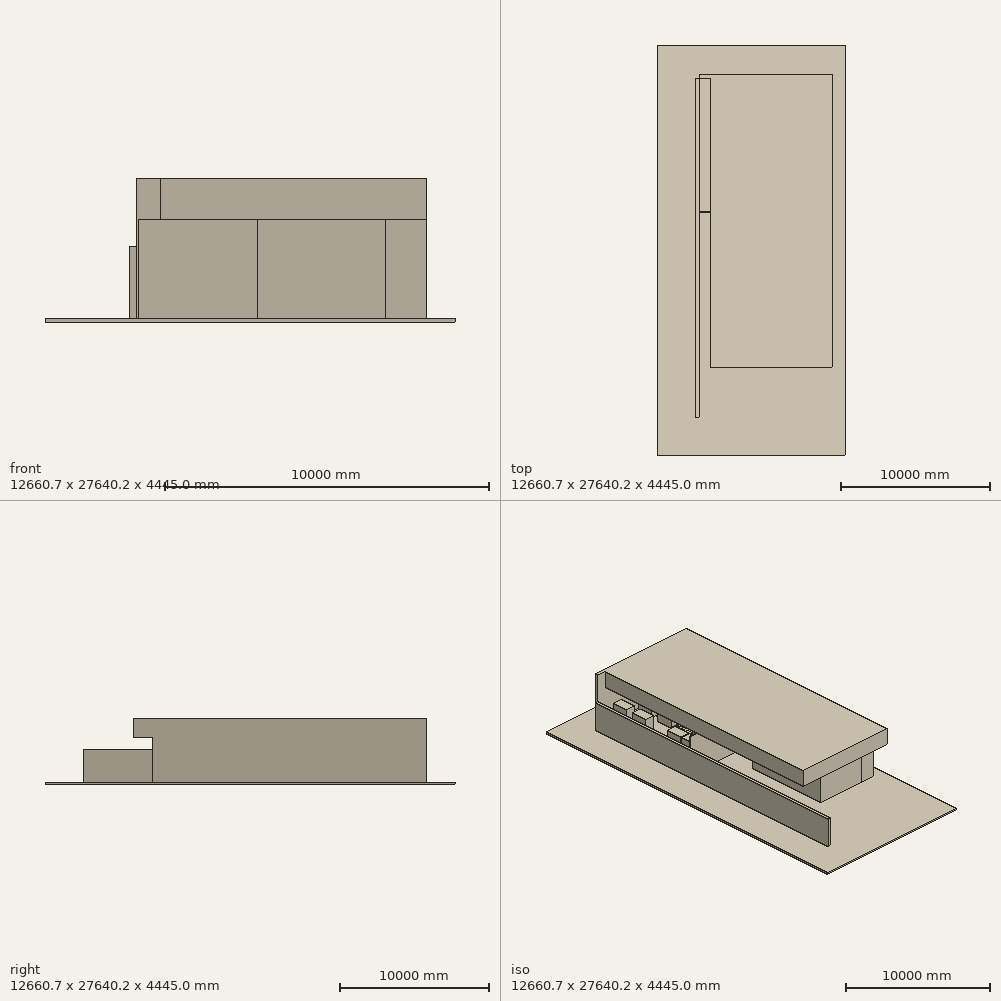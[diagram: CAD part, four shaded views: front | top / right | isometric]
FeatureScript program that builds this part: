
annotation { "Feature Type Name" : "Feature", "Feature Type Description" : "" }
export const myFeature = defineFeature(function(context is Context, id is Id, definition is map)
    precondition{}
    {
        {
            var Q0;
            Q0=qCreatedBy(makeId("Top.planeOp"),FACE);
            var sketch = newSketch(context, id + "F0", { "sketchPlane" : qUnion([Q0])});
            skLineSegment(sketch, "E0.bottom", {"start": v(0, 0) * mm, "end": v(3962.4, 0) * mm});
            skLineSegment(sketch, "E0.right", {"start": v(3962.4, 0) * mm, "end": v(3962.4, 100.58) * mm});
            skLineSegment(sketch, "E1.bottom", {"start": v(0, -9144) * mm, "end": v(3962.4, -9144) * mm});
            skLineSegment(sketch, "E1.top", {"start": v(0, -2438.4) * mm, "end": v(3962.4, -2438.4) * mm});
            skLineSegment(sketch, "E1.left", {"start": v(0, -2438.4) * mm, "end": v(0, -9144) * mm});
            skLineSegment(sketch, "E1.right", {"start": v(3962.4, -2438.4) * mm, "end": v(3962.4, -9144) * mm});
            skLineSegment(sketch, "E2", {"start": v(0, 100.58) * mm, "end": v(3962.4, 100.58) * mm});
            skLineSegment(sketch, "E3", {"start": v(0, 0) * mm, "end": v(0, 100.58) * mm});
            skLineSegment(sketch, "E4", {"start": v(0, 0) * mm, "end": v(-3657.6, 0) * mm});
            skLineSegment(sketch, "E5", {"start": v(-3657.6, 0) * mm, "end": v(-3657.6, 100.58) * mm});
            skLineSegment(sketch, "E6", {"start": v(-3657.6, 100.58) * mm, "end": v(0, 100.58) * mm});
            skSolve(sketch);
        }
        {
            var Q0;
            Q0=qSketchRegion(id+"F0",true);
            extrude(context, id + "F1", {"entities" : qUnion([Q0]), "depth" : 3048 * mm});
        }
        {
            var Q0;
            Q0=qCreatedBy(makeId("Top.planeOp"),FACE);
            var sketch = newSketch(context, id + "F2", { "sketchPlane" : qUnion([Q0])});
            skLineSegment(sketch, "E7.bottom", {"start": v(-3718.56, 9040.37) * mm, "end": v(3962.4, 9040.37) * mm});
            skLineSegment(sketch, "E7.top", {"start": v(-3718.56, 9284.2) * mm, "end": v(3962.4, 9284.2) * mm});
            skLineSegment(sketch, "E7.left", {"start": v(-3718.56, 9040.37) * mm, "end": v(-3718.56, 9284.2) * mm});
            skLineSegment(sketch, "E7.right", {"start": v(3962.4, 9040.37) * mm, "end": v(3962.4, 9284.2) * mm});
            skLineSegment(sketch, "E8.bottom", {"start": v(-3718.56, 9040.37) * mm, "end": v(-3962.4, 9040.37) * mm});
            skLineSegment(sketch, "E8.top", {"start": v(-3718.56, -13819.63) * mm, "end": v(-3962.4, -13819.63) * mm});
            skLineSegment(sketch, "E8.left", {"start": v(-3718.56, 9040.37) * mm, "end": v(-3718.56, -13819.63) * mm});
            skLineSegment(sketch, "E8.right", {"start": v(-3962.4, 9040.37) * mm, "end": v(-3962.4, -13819.63) * mm});
            skSolve(sketch);
        }
        {
            var Q0;
            Q0=qSketchRegion(id+"F2",true);
            extrude(context, id + "F3", {"entities" : qUnion([Q0]), "depth" : 2212.85 * mm});
        }
        {
            var Q0;
            Q0=makeQuery(id+"F1.opExtrude","CAP_FACE",FACE,{"disambiguationData":[OSD([sQuery(id+"F0.wireOp",EDGE,"E0.bottom"),sQuery(id+"F0.wireOp",EDGE,"E0.top"),sQuery(id+"F0.wireOp",EDGE,"E0.left"),sQuery(id+"F0.wireOp",EDGE,"E0.right")])],"isStart":false});
            var sketch = newSketch(context, id + "F4", { "sketchPlane" : qUnion([Q0])});
            skLineSegment(sketch, "E9.bottom", {"start": v(3962.4, 9284.2) * mm, "end": v(-2990.09, 9284.2) * mm});
            skLineSegment(sketch, "E9.top", {"start": v(3962.4, -10436.35) * mm, "end": v(-2990.09, -10436.35) * mm});
            skLineSegment(sketch, "E9.left", {"start": v(3962.4, 9284.2) * mm, "end": v(3962.4, -10436.35) * mm});
            skLineSegment(sketch, "E9.right", {"start": v(-2990.09, 9284.2) * mm, "end": v(-2990.09, -10436.35) * mm});
            skSolve(sketch);
        }
        {
            var Q0;
            Q0=qSketchRegion(id+"F4",true);
            extrude(context, id + "F5", {"entities" : qUnion([Q0]), "depth" : 1270 * mm});
        }
        {
            var Q0;
            Q0=makeQuery(id+"F1.opExtrude","SWEPT_FACE",FACE,{"disambiguationData":[OSD([sQuery(id+"F0.wireOp",EDGE,"E1.right")])]});
            var sketch = newSketch(context, id + "F6", { "sketchPlane" : qUnion([Q0])});
            skLineSegment(sketch, "E10.bottom", {"start": v(-9144, 0) * mm, "end": v(9284.2, 0) * mm});
            skLineSegment(sketch, "E10.top", {"start": v(-9144, 4318) * mm, "end": v(9284.2, 4318) * mm});
            skLineSegment(sketch, "E10.left", {"start": v(-9144, 0) * mm, "end": v(-9144, 3048) * mm});
            skLineSegment(sketch, "E10.right", {"start": v(9284.2, 0) * mm, "end": v(9284.2, 4318) * mm});
            skLineSegment(sketch, "E11.bottom", {"start": v(-9144, 4318) * mm, "end": v(-10436.35, 4318) * mm});
            skLineSegment(sketch, "E11.top", {"start": v(-9144, 3048) * mm, "end": v(-10436.35, 3048) * mm});
            skLineSegment(sketch, "E11.right", {"start": v(-10436.35, 4318) * mm, "end": v(-10436.35, 3048) * mm});
            skSolve(sketch);
        }
        {
            var Q0;
            Q0=qSketchRegion(id+"F6",true);
            extrude(context, id + "F7", {"entities" : qUnion([Q0]), "depth" : 1270 * mm});
        }
        {
            var Q0;
            Q0=qCreatedBy(makeId("Top.planeOp"),FACE);
            var sketch = newSketch(context, id + "F8", { "sketchPlane" : qUnion([Q0])});
            skLineSegment(sketch, "E12.bottom", {"start": v(6117.86, 11268.55) * mm, "end": v(-6542.87, 11268.55) * mm});
            skLineSegment(sketch, "E12.top", {"start": v(6117.86, -16371.62) * mm, "end": v(-6542.87, -16371.62) * mm});
            skLineSegment(sketch, "E12.left", {"start": v(6117.86, 11268.55) * mm, "end": v(6117.86, -16371.62) * mm});
            skLineSegment(sketch, "E12.right", {"start": v(-6542.87, 11268.55) * mm, "end": v(-6542.87, -16371.62) * mm});
            skSolve(sketch);
        }
        {
            var Q0;
            Q0=qSketchRegion(id+"F8",true);
            extrude(context, id + "F9", {"entities" : qUnion([Q0]), "oppositeDirection" : true, "depth" : 127 * mm});
        }
        {
            var Q0;
            Q0=makeQuery(id+"F3.opExtrude","CAP_FACE",FACE,{"disambiguationData":[OSD([sQuery(id+"F2.wireOp",EDGE,"E7.bottom"),sQuery(id+"F2.wireOp",EDGE,"E7.top"),sQuery(id+"F2.wireOp",EDGE,"E7.left"),sQuery(id+"F2.wireOp",EDGE,"E7.right")])],"isStart":false});
            var sketch = newSketch(context, id + "F10", { "sketchPlane" : qUnion([Q0])});
            skLineSegment(sketch, "E13.bottom", {"start": v(-3718.56, 9284.2) * mm, "end": v(3962.4, 9284.2) * mm});
            skLineSegment(sketch, "E13.top", {"start": v(-3718.56, 9040.37) * mm, "end": v(3962.4, 9040.37) * mm});
            skLineSegment(sketch, "E13.left", {"start": v(-3718.56, 9284.2) * mm, "end": v(-3718.56, 9040.37) * mm});
            skLineSegment(sketch, "E13.right", {"start": v(3962.4, 9284.2) * mm, "end": v(3962.4, 9040.37) * mm});
            skSolve(sketch);
        }
        {
            var Q0;
            Q0=qSketchRegion(id+"F10",true);
            var Q1;
            Q1=makeQuery(id+"F5.opExtrude","CAP_FACE",FACE,{"disambiguationData":[OSD([sQuery(id+"F4.wireOp",EDGE,"E9.bottom"),sQuery(id+"F4.wireOp",EDGE,"E9.top"),sQuery(id+"F4.wireOp",EDGE,"E9.left"),sQuery(id+"F4.wireOp",EDGE,"E9.right")])],"isStart":false});
            extrude(context, id + "F11", {"entities" : qUnion([Q0]), "operationType" : NewBodyOperationType.ADD, "endBound" : BoundingType.UP_TO_SURFACE, "endBoundEntityFace" : qUnion([Q1]), "depth" : 25.4 * mm});
        }
        {
            var Q0;
            Q0=qCreatedBy(makeId("Top.planeOp"),FACE);
            var sketch = newSketch(context, id + "F12", { "sketchPlane" : qUnion([Q0])});
            skLineSegment(sketch, "E14.bottom", {"start": v(-2499.36, 710.18) * mm, "end": v(-1724.66, 710.18) * mm});
            skLineSegment(sketch, "E14.top", {"start": v(-2499.36, 2005.58) * mm, "end": v(-1724.66, 2005.58) * mm});
            skLineSegment(sketch, "E14.left", {"start": v(-2499.36, 710.18) * mm, "end": v(-2499.36, 2005.58) * mm});
            skLineSegment(sketch, "E14.right", {"start": v(-1724.66, 710.18) * mm, "end": v(-1724.66, 2005.58) * mm});
            skLineSegment(sketch, "E15.bottom", {"start": v(-2499.36, 2107.18) * mm, "end": v(-1724.66, 2107.18) * mm});
            skLineSegment(sketch, "E15.top", {"start": v(-2499.36, 3402.58) * mm, "end": v(-1724.66, 3402.58) * mm});
            skLineSegment(sketch, "E15.left", {"start": v(-2499.36, 2107.18) * mm, "end": v(-2499.36, 3402.58) * mm});
            skLineSegment(sketch, "E15.right", {"start": v(-1724.66, 2107.18) * mm, "end": v(-1724.66, 3402.58) * mm});
            skLineSegment(sketch, "E16.bottom", {"start": v(-2499.36, 5535.17) * mm, "end": v(-1724.66, 5535.17) * mm});
            skLineSegment(sketch, "E16.top", {"start": v(-2499.36, 6830.57) * mm, "end": v(-1724.66, 6830.57) * mm});
            skLineSegment(sketch, "E16.left", {"start": v(-2499.36, 5535.17) * mm, "end": v(-2499.36, 6830.57) * mm});
            skLineSegment(sketch, "E16.right", {"start": v(-1724.66, 5535.17) * mm, "end": v(-1724.66, 6830.57) * mm});
            skLineSegment(sketch, "E17.bottom", {"start": v(-35.56, 6830.57) * mm, "end": v(739.14, 6830.57) * mm});
            skLineSegment(sketch, "E17.top", {"start": v(-35.56, 5535.17) * mm, "end": v(739.14, 5535.17) * mm});
            skLineSegment(sketch, "E17.left", {"start": v(-35.56, 6830.57) * mm, "end": v(-35.56, 5535.17) * mm});
            skLineSegment(sketch, "E17.right", {"start": v(739.14, 6830.57) * mm, "end": v(739.14, 5535.17) * mm});
            skLineSegment(sketch, "E18.bottom", {"start": v(-35.56, 3402.58) * mm, "end": v(739.14, 3402.58) * mm});
            skLineSegment(sketch, "E18.top", {"start": v(-35.56, 2107.18) * mm, "end": v(739.14, 2107.18) * mm});
            skLineSegment(sketch, "E18.left", {"start": v(-35.56, 3402.58) * mm, "end": v(-35.56, 2107.18) * mm});
            skLineSegment(sketch, "E18.right", {"start": v(739.14, 3402.58) * mm, "end": v(739.14, 2107.18) * mm});
            skLineSegment(sketch, "E19.bottom", {"start": v(-35.56, 2005.58) * mm, "end": v(739.14, 2005.58) * mm});
            skLineSegment(sketch, "E19.top", {"start": v(-35.56, 710.18) * mm, "end": v(739.14, 710.18) * mm});
            skLineSegment(sketch, "E19.left", {"start": v(-35.56, 2005.58) * mm, "end": v(-35.56, 710.18) * mm});
            skLineSegment(sketch, "E19.right", {"start": v(739.14, 2005.58) * mm, "end": v(739.14, 710.18) * mm});
            skLineSegment(sketch, "E20.bottom", {"start": v(2665.63, 7031.21) * mm, "end": v(3414.93, 7031.21) * mm});
            skLineSegment(sketch, "E20.top", {"start": v(2665.63, 8631.41) * mm, "end": v(3414.93, 8631.41) * mm});
            skLineSegment(sketch, "E20.left", {"start": v(2665.63, 7031.21) * mm, "end": v(2665.63, 8631.41) * mm});
            skLineSegment(sketch, "E20.right", {"start": v(3414.93, 7031.21) * mm, "end": v(3414.93, 8631.41) * mm});
            skLineSegment(sketch, "E21.bottom", {"start": v(-2499.36, 7440.17) * mm, "end": v(-1724.66, 7440.17) * mm});
            skLineSegment(sketch, "E21.top", {"start": v(-2499.36, 8735.57) * mm, "end": v(-1724.66, 8735.57) * mm});
            skLineSegment(sketch, "E21.left", {"start": v(-2499.36, 7440.17) * mm, "end": v(-2499.36, 8735.57) * mm});
            skLineSegment(sketch, "E21.right", {"start": v(-1724.66, 7440.17) * mm, "end": v(-1724.66, 8735.57) * mm});
            skLineSegment(sketch, "E22.bottom", {"start": v(-35.56, 7440.17) * mm, "end": v(739.14, 7440.17) * mm});
            skLineSegment(sketch, "E22.top", {"start": v(-35.56, 8735.57) * mm, "end": v(739.14, 8735.57) * mm});
            skLineSegment(sketch, "E22.left", {"start": v(-35.56, 7440.17) * mm, "end": v(-35.56, 8735.57) * mm});
            skLineSegment(sketch, "E22.right", {"start": v(739.14, 7440.17) * mm, "end": v(739.14, 8735.57) * mm});
            skLineSegment(sketch, "E23", {"start": v(-2004.06, 963.1) * mm, "end": v(-2004.06, 3910.58) * mm});
            skArc(sketch, "E24", {"start": v(-2004.06, 3910.58) * mm, "mid": v(-1922.23, 4108.15) * mm, "end": v(-1724.66, 4189.98) * mm});
            skLineSegment(sketch, "E25", {"start": v(-2004.06, 963.1) * mm, "end": v(-1800.86, 963.1) * mm});
            skLineSegment(sketch, "E26", {"start": v(-1800.86, 963.1) * mm, "end": v(-1800.86, 3910.58) * mm});
            skArc(sketch, "E27", {"start": v(-1800.86, 3910.58) * mm, "mid": v(-1778.54, 3964.47) * mm, "end": v(-1724.66, 3986.78) * mm});
            skLineSegment(sketch, "E28", {"start": v(-1724.66, 3986.78) * mm, "end": v(3872.3, 3986.78) * mm});
            skLineSegment(sketch, "E29", {"start": v(-1724.66, 4189.98) * mm, "end": v(3872.3, 4189.98) * mm});
            skLineSegment(sketch, "E30", {"start": v(-1778.54, 3964.47) * mm, "end": v(-1922.23, 4108.15) * mm, "construction": true});
            skLineSegment(sketch, "E31", {"start": v(-2423.16, 3139.03) * mm, "end": v(-2219.96, 3139.03) * mm});
            skLineSegment(sketch, "E32", {"start": v(-2219.96, 3139.03) * mm, "end": v(-2219.96, 4139.18) * mm});
            skArc(sketch, "E33", {"start": v(-2219.96, 4139.18) * mm, "mid": v(-2197.64, 4193.07) * mm, "end": v(-2143.76, 4215.38) * mm});
            skLineSegment(sketch, "E34", {"start": v(-2423.16, 3139.03) * mm, "end": v(-2423.16, 4139.18) * mm});
            skArc(sketch, "E35", {"start": v(-2423.16, 4139.18) * mm, "mid": v(-2341.33, 4336.75) * mm, "end": v(-2143.76, 4418.58) * mm});
            skLineSegment(sketch, "E36", {"start": v(-2143.76, 4215.38) * mm, "end": v(3879.27, 4215.38) * mm});
            skLineSegment(sketch, "E37", {"start": v(3879.27, 4215.38) * mm, "end": v(3879.27, 4418.58) * mm});
            skLineSegment(sketch, "E38", {"start": v(3879.27, 4418.58) * mm, "end": v(-2143.76, 4418.58) * mm});
            skLineSegment(sketch, "E39", {"start": v(-2197.64, 4193.07) * mm, "end": v(-2341.33, 4336.75) * mm, "construction": true});
            skLineSegment(sketch, "E40", {"start": v(459.74, 993.21) * mm, "end": v(459.74, 3453.38) * mm});
            skArc(sketch, "E41", {"start": v(459.74, 3453.38) * mm, "mid": v(541.57, 3650.95) * mm, "end": v(739.14, 3732.78) * mm});
            skLineSegment(sketch, "E42", {"start": v(459.74, 993.21) * mm, "end": v(662.94, 993.21) * mm});
            skLineSegment(sketch, "E43", {"start": v(662.94, 993.21) * mm, "end": v(662.94, 3453.38) * mm});
            skArc(sketch, "E44", {"start": v(662.94, 3453.38) * mm, "mid": v(685.26, 3507.27) * mm, "end": v(739.14, 3529.58) * mm});
            skLineSegment(sketch, "E45", {"start": v(739.14, 3529.58) * mm, "end": v(3914.38, 3529.58) * mm});
            skLineSegment(sketch, "E46", {"start": v(739.14, 3732.78) * mm, "end": v(3914.38, 3732.78) * mm});
            skLineSegment(sketch, "E47", {"start": v(685.26, 3507.27) * mm, "end": v(541.57, 3650.95) * mm, "construction": true});
            skLineSegment(sketch, "E48", {"start": v(40.64, 3024.4) * mm, "end": v(243.84, 3024.4) * mm});
            skLineSegment(sketch, "E49", {"start": v(243.84, 3024.4) * mm, "end": v(243.84, 3681.98) * mm});
            skArc(sketch, "E50", {"start": v(243.84, 3681.98) * mm, "mid": v(266.16, 3735.87) * mm, "end": v(320.04, 3758.18) * mm});
            skLineSegment(sketch, "E51", {"start": v(40.64, 3024.4) * mm, "end": v(40.64, 3681.98) * mm});
            skArc(sketch, "E52", {"start": v(40.64, 3681.98) * mm, "mid": v(122.47, 3879.55) * mm, "end": v(320.04, 3961.38) * mm});
            skLineSegment(sketch, "E53", {"start": v(320.04, 3758.18) * mm, "end": v(3899.59, 3758.18) * mm});
            skLineSegment(sketch, "E54", {"start": v(3899.59, 3758.18) * mm, "end": v(3899.59, 3961.38) * mm});
            skLineSegment(sketch, "E55", {"start": v(3899.59, 3961.38) * mm, "end": v(320.04, 3961.38) * mm});
            skLineSegment(sketch, "E56", {"start": v(266.16, 3735.87) * mm, "end": v(122.47, 3879.55) * mm, "construction": true});
            skLineSegment(sketch, "E57", {"start": v(3914.38, 3732.78) * mm, "end": v(3914.38, 3529.58) * mm});
            skLineSegment(sketch, "E58", {"start": v(3872.3, 3986.78) * mm, "end": v(3872.3, 4189.98) * mm});
            skLineSegment(sketch, "E59", {"start": v(-1832.37, 4443.98) * mm, "end": v(4264.41, 4443.98) * mm});
            skArc(sketch, "E60.MirrorCS", {"start": v(-2219.96, 4748.78) * mm, "mid": v(-2197.64, 4694.9) * mm, "end": v(-2143.76, 4672.58) * mm});
            skArc(sketch, "E61.MirrorCS", {"start": v(662.94, 5434.58) * mm, "mid": v(685.26, 5380.7) * mm, "end": v(739.14, 5358.38) * mm});
            skArc(sketch, "E62.MirrorCS", {"start": v(243.84, 5205.98) * mm, "mid": v(266.16, 5152.1) * mm, "end": v(320.04, 5129.78) * mm});
            skLineSegment(sketch, "E63.MirrorCS", {"start": v(3899.59, 5129.78) * mm, "end": v(3899.59, 4926.58) * mm});
            skLineSegment(sketch, "E64.MirrorCS", {"start": v(3879.27, 4672.58) * mm, "end": v(3879.27, 4469.38) * mm});
            skLineSegment(sketch, "E65.MirrorCS", {"start": v(3914.38, 5155.18) * mm, "end": v(3914.38, 5358.38) * mm});
            skLineSegment(sketch, "E66.MirrorCS", {"start": v(685.26, 5380.7) * mm, "end": v(541.57, 5237.02) * mm, "construction": true});
            skArc(sketch, "E67.MirrorCS", {"start": v(40.64, 5205.98) * mm, "mid": v(122.47, 5008.42) * mm, "end": v(320.04, 4926.58) * mm});
            skLineSegment(sketch, "E68.MirrorCS", {"start": v(-2143.76, 4672.58) * mm, "end": v(-611.16, 4672.58) * mm});
            skLineSegment(sketch, "E69.MirrorCS", {"start": v(-2197.64, 4694.9) * mm, "end": v(-2341.33, 4551.22) * mm, "construction": true});
            skArc(sketch, "E70.MirrorCS", {"start": v(-2423.16, 4748.78) * mm, "mid": v(-2341.33, 4551.22) * mm, "end": v(-2143.76, 4469.38) * mm});
            skLineSegment(sketch, "E71.MirrorCS", {"start": v(266.16, 5152.1) * mm, "end": v(122.47, 5008.42) * mm, "construction": true});
            skArc(sketch, "E72.MirrorCS", {"start": v(459.74, 5434.58) * mm, "mid": v(541.57, 5237.02) * mm, "end": v(739.14, 5155.18) * mm});
            skLineSegment(sketch, "E73.MirrorCS", {"start": v(320.04, 5129.78) * mm, "end": v(3899.59, 5129.78) * mm});
            skLineSegment(sketch, "E74.MirrorCS", {"start": v(739.14, 5155.18) * mm, "end": v(3914.38, 5155.18) * mm});
            skLineSegment(sketch, "E75.MirrorCS", {"start": v(3879.27, 4469.38) * mm, "end": v(-2143.76, 4469.38) * mm});
            skLineSegment(sketch, "E76.MirrorCS", {"start": v(739.14, 5358.38) * mm, "end": v(3914.38, 5358.38) * mm});
            skLineSegment(sketch, "E77.MirrorCS", {"start": v(3899.59, 4926.58) * mm, "end": v(320.04, 4926.58) * mm});
            skLineSegment(sketch, "E78", {"start": v(-2423.16, 4748.78) * mm, "end": v(-2423.16, 6609.89) * mm});
            skLineSegment(sketch, "E79", {"start": v(-2423.16, 6609.89) * mm, "end": v(-2219.96, 6609.89) * mm});
            skLineSegment(sketch, "E80", {"start": v(-2219.96, 6609.89) * mm, "end": v(-2219.96, 4748.78) * mm});
            skLineSegment(sketch, "E81", {"start": v(40.64, 5205.98) * mm, "end": v(40.64, 6602.13) * mm});
            skLineSegment(sketch, "E82", {"start": v(40.64, 6602.13) * mm, "end": v(243.84, 6602.13) * mm});
            skLineSegment(sketch, "E83", {"start": v(243.84, 6602.13) * mm, "end": v(243.84, 5205.98) * mm});
            skLineSegment(sketch, "E84", {"start": v(459.74, 5434.58) * mm, "end": v(459.74, 7694.34) * mm});
            skLineSegment(sketch, "E85", {"start": v(459.74, 7694.34) * mm, "end": v(662.94, 7694.34) * mm});
            skLineSegment(sketch, "E86", {"start": v(662.94, 7694.34) * mm, "end": v(662.94, 5434.58) * mm});
            skLineSegment(sketch, "E87", {"start": v(-1817.3, 7728.89) * mm, "end": v(-2020.5, 7728.89) * mm});
            skLineSegment(sketch, "E88", {"start": v(-2020.5, 7728.89) * mm, "end": v(-2020.5, 5361.81) * mm});
            skLineSegment(sketch, "E89", {"start": v(-1817.3, 7728.89) * mm, "end": v(-1817.3, 5361.81) * mm});
            skArc(sketch, "E90", {"start": v(-2020.5, 5361.81) * mm, "mid": v(-1890.04, 5046.85) * mm, "end": v(-1575.08, 4916.4) * mm});
            skArc(sketch, "E91", {"start": v(-1817.3, 5361.81) * mm, "mid": v(-1746.36, 5190.54) * mm, "end": v(-1575.08, 5119.6) * mm});
            skLineSegment(sketch, "E92", {"start": v(-1575.08, 4916.4) * mm, "end": v(-1413.46, 4916.4) * mm});
            skLineSegment(sketch, "E93", {"start": v(-1575.08, 5119.6) * mm, "end": v(-1383.27, 5119.6) * mm});
            skLineSegment(sketch, "E94", {"start": v(-1746.36, 5190.54) * mm, "end": v(-1890.04, 5046.85) * mm, "construction": true});
            skLineSegment(sketch, "E95", {"start": v(-1727.68, 5119.6) * mm, "end": v(-1727.68, 4916.4) * mm, "construction": true});
            skPoint(sketch, "E95.endSnap0", {"position": v(-1494.27, 4916.4) * mm});
            skLineSegment(sketch, "E96", {"start": v(-1413.46, 4916.4) * mm, "end": v(-611.16, 4672.58) * mm});
            skLineSegment(sketch, "E97", {"start": v(-1383.27, 5119.6) * mm, "end": v(87.7, 4672.58) * mm});
            skLineSegment(sketch, "E98", {"start": v(-606.43, 4671.15) * mm, "end": v(-547.34, 4865.57) * mm, "construction": true});
            skLineSegment(sketch, "E99.trimOffspring", {"start": v(87.7, 4672.58) * mm, "end": v(3879.27, 4672.58) * mm});
            skSolve(sketch);
        }
        {
            var Q0;
            Q0=makeQuery(id+"F12.imprint","IMPRINT",FACE,{"disambiguationData":[TD([[makeQuery(id+"F12.imprint","IMPRINT",EDGE,{"derivedFrom":sQuery(id+"F12.wireOp",EDGE,"E14.bottom")}),1.0]])]});
            var Q1;
            {var subQ5=sQuery(id+"F12.wireOp",EDGE,"E25");Q1=makeQuery(id+"F12.imprint","IMPRINT",FACE,{"disambiguationData":[TD([[makeQuery(id+"F12.imprint","IMPRINT",EDGE,{"derivedFrom":subQ5}),1.0]])]});}
            var Q2;
            {var subQ0=sQuery(id+"F12.wireOp",EDGE,"E15.left");Q2=makeQuery(id+"F12.imprint","IMPRINT",FACE,{"disambiguationData":[TD([[makeQuery(id+"F12.imprint","IMPRINT",EDGE,{"derivedFrom":subQ0}),-1.0]])]});}
            var Q3;
            {var subQ5=sQuery(id+"F12.wireOp",EDGE,"E31");Q3=makeQuery(id+"F12.imprint","IMPRINT",FACE,{"disambiguationData":[TD([[makeQuery(id+"F12.imprint","IMPRINT",EDGE,{"derivedFrom":subQ5}),1.0]])]});}
            var Q4;
            {var subQ0=sQuery(id+"F12.wireOp",EDGE,"E23");var subQ1=sQuery(id+"F12.wireOp",EDGE,"E15.bottom");var subQ2=makeQuery(id+"F12.imprint","INTERSECT",VERTEX,{"derivedFrom":[subQ1,subQ0]});Q4=makeQuery(id+"F12.imprint","IMPRINT",FACE,{"disambiguationData":[TD([[makeQuery(id+"F12.imprint","IMPRINT",EDGE,{"disambiguationData":[TD([[subQ2,-1.0]])],"derivedFrom":subQ1}),1.0]])]});}
            var Q5;
            {var subQ0=sQuery(id+"F12.wireOp",EDGE,"E15.right");Q5=makeQuery(id+"F12.imprint","IMPRINT",FACE,{"disambiguationData":[TD([[makeQuery(id+"F12.imprint","IMPRINT",EDGE,{"derivedFrom":subQ0}),1.0]])]});}
            var Q6;
            {var subQ0=sQuery(id+"F12.wireOp",EDGE,"E16.left");Q6=makeQuery(id+"F12.imprint","IMPRINT",FACE,{"disambiguationData":[TD([[makeQuery(id+"F12.imprint","IMPRINT",EDGE,{"derivedFrom":subQ0}),-1.0]])]});}
            var Q7;
            {var subQ5=sQuery(id+"F12.wireOp",EDGE,"E79");Q7=makeQuery(id+"F12.imprint","IMPRINT",FACE,{"disambiguationData":[TD([[makeQuery(id+"F12.imprint","IMPRINT",EDGE,{"derivedFrom":subQ5}),-1.0]])]});}
            var Q8;
            {var subQ0=sQuery(id+"F12.wireOp",EDGE,"E16.right");Q8=makeQuery(id+"F12.imprint","IMPRINT",FACE,{"disambiguationData":[TD([[makeQuery(id+"F12.imprint","IMPRINT",EDGE,{"derivedFrom":subQ0}),1.0]])]});}
            var Q9;
            {var subQ0=sQuery(id+"F12.wireOp",EDGE,"E89");var subQ1=sQuery(id+"F12.wireOp",EDGE,"E16.bottom");var subQ2=makeQuery(id+"F12.imprint","INTERSECT",VERTEX,{"derivedFrom":[subQ1,subQ0]});Q9=makeQuery(id+"F12.imprint","IMPRINT",FACE,{"disambiguationData":[TD([[makeQuery(id+"F12.imprint","IMPRINT",EDGE,{"disambiguationData":[TD([[subQ2,1.0]])],"derivedFrom":subQ1}),1.0]])]});}
            var Q10;
            Q10=makeQuery(id+"F12.imprint","IMPRINT",FACE,{"disambiguationData":[TD([[makeQuery(id+"F12.imprint","IMPRINT",EDGE,{"derivedFrom":sQuery(id+"F12.wireOp",EDGE,"E21.top")}),-1.0]])]});
            var Q11;
            {var subQ5=sQuery(id+"F12.wireOp",EDGE,"E87");Q11=makeQuery(id+"F12.imprint","IMPRINT",FACE,{"disambiguationData":[TD([[makeQuery(id+"F12.imprint","IMPRINT",EDGE,{"derivedFrom":subQ5}),1.0]])]});}
            var Q12;
            Q12=makeQuery(id+"F12.imprint","IMPRINT",FACE,{"disambiguationData":[TD([[makeQuery(id+"F12.imprint","IMPRINT",EDGE,{"derivedFrom":sQuery(id+"F12.wireOp",EDGE,"E19.top")}),1.0]])]});
            var Q13;
            {var subQ5=sQuery(id+"F12.wireOp",EDGE,"E42");Q13=makeQuery(id+"F12.imprint","IMPRINT",FACE,{"disambiguationData":[TD([[makeQuery(id+"F12.imprint","IMPRINT",EDGE,{"derivedFrom":subQ5}),1.0]])]});}
            var Q14;
            {var subQ0=sQuery(id+"F12.wireOp",EDGE,"E18.left");Q14=makeQuery(id+"F12.imprint","IMPRINT",FACE,{"disambiguationData":[TD([[makeQuery(id+"F12.imprint","IMPRINT",EDGE,{"derivedFrom":subQ0}),1.0]])]});}
            var Q15;
            {var subQ5=sQuery(id+"F12.wireOp",EDGE,"E48");Q15=makeQuery(id+"F12.imprint","IMPRINT",FACE,{"disambiguationData":[TD([[makeQuery(id+"F12.imprint","IMPRINT",EDGE,{"derivedFrom":subQ5}),1.0]])]});}
            var Q16;
            {var subQ0=sQuery(id+"F12.wireOp",EDGE,"E18.right");Q16=makeQuery(id+"F12.imprint","IMPRINT",FACE,{"disambiguationData":[TD([[makeQuery(id+"F12.imprint","IMPRINT",EDGE,{"derivedFrom":subQ0}),-1.0]])]});}
            var Q17;
            {var subQ0=sQuery(id+"F12.wireOp",EDGE,"E40");var subQ1=sQuery(id+"F12.wireOp",EDGE,"E18.bottom");var subQ2=makeQuery(id+"F12.imprint","INTERSECT",VERTEX,{"derivedFrom":[subQ1,subQ0]});Q17=makeQuery(id+"F12.imprint","IMPRINT",FACE,{"disambiguationData":[TD([[makeQuery(id+"F12.imprint","IMPRINT",EDGE,{"disambiguationData":[TD([[subQ2,-1.0]])],"derivedFrom":subQ1}),-1.0]])]});}
            var Q18;
            {var subQ5=sQuery(id+"F12.wireOp",EDGE,"E82");Q18=makeQuery(id+"F12.imprint","IMPRINT",FACE,{"disambiguationData":[TD([[makeQuery(id+"F12.imprint","IMPRINT",EDGE,{"derivedFrom":subQ5}),-1.0]])]});}
            var Q19;
            {var subQ0=sQuery(id+"F12.wireOp",EDGE,"E17.left");Q19=makeQuery(id+"F12.imprint","IMPRINT",FACE,{"disambiguationData":[TD([[makeQuery(id+"F12.imprint","IMPRINT",EDGE,{"derivedFrom":subQ0}),1.0]])]});}
            var Q20;
            {var subQ0=sQuery(id+"F12.wireOp",EDGE,"E84");var subQ1=sQuery(id+"F12.wireOp",EDGE,"E17.bottom");var subQ2=makeQuery(id+"F12.imprint","INTERSECT",VERTEX,{"derivedFrom":[subQ1,subQ0]});Q20=makeQuery(id+"F12.imprint","IMPRINT",FACE,{"disambiguationData":[TD([[makeQuery(id+"F12.imprint","IMPRINT",EDGE,{"disambiguationData":[TD([[subQ2,-1.0]])],"derivedFrom":subQ1}),-1.0]])]});}
            var Q21;
            {var subQ0=sQuery(id+"F12.wireOp",EDGE,"E17.right");Q21=makeQuery(id+"F12.imprint","IMPRINT",FACE,{"disambiguationData":[TD([[makeQuery(id+"F12.imprint","IMPRINT",EDGE,{"derivedFrom":subQ0}),-1.0]])]});}
            var Q22;
            Q22=makeQuery(id+"F12.imprint","IMPRINT",FACE,{"disambiguationData":[TD([[makeQuery(id+"F12.imprint","IMPRINT",EDGE,{"derivedFrom":sQuery(id+"F12.wireOp",EDGE,"E22.top")}),-1.0]])]});
            var Q23;
            {var subQ5=sQuery(id+"F12.wireOp",EDGE,"E85");Q23=makeQuery(id+"F12.imprint","IMPRINT",FACE,{"disambiguationData":[TD([[makeQuery(id+"F12.imprint","IMPRINT",EDGE,{"derivedFrom":subQ5}),-1.0]])]});}
            var Q24;
            Q24=makeQuery(id+"F12.imprint","IMPRINT",FACE,{"disambiguationData":[TD([[makeQuery(id+"F12.imprint","IMPRINT",EDGE,{"derivedFrom":sQuery(id+"F12.wireOp",EDGE,"E20.bottom")}),1.0]])]});
            extrude(context, id + "F13", {"entities" : qUnion([Q0, Q1, Q2, Q3, Q4, Q5, Q6, Q7, Q8, Q9, Q10, Q11, Q12, Q13, Q14, Q15, Q16, Q17, Q18, Q19, Q20, Q21, Q22, Q23, Q24]), "depth" : 1695.45 * mm});
        }
        {
            var Q0;
            Q0=qCreatedBy(makeId("Top.planeOp"),FACE);
            var sketch = newSketch(context, id + "F14", { "sketchPlane" : qUnion([Q0])});
            skLineSegment(sketch, "E100.bottom", {"start": v(607.65, 7254.54) * mm, "end": v(3668.35, 7254.54) * mm});
            skLineSegment(sketch, "E100.top", {"start": v(607.65, 5165.39) * mm, "end": v(3668.35, 5165.39) * mm});
            skLineSegment(sketch, "E100.left", {"start": v(607.65, 7254.54) * mm, "end": v(607.65, 5165.39) * mm});
            skLineSegment(sketch, "E100.right", {"start": v(3668.35, 7254.54) * mm, "end": v(3668.35, 5165.39) * mm});
            skSolve(sketch);
        }
        {
            var Q0;
            Q0=qCreatedBy(makeId("Top.planeOp"),FACE);
            var sketch = newSketch(context, id + "F15", { "sketchPlane" : qUnion([Q0])});
            skLineSegment(sketch, "E101.bottom", {"start": v(1227.74, 8964) * mm, "end": v(478.44, 8964) * mm});
            skLineSegment(sketch, "E101.top", {"start": v(1227.74, 7363.8) * mm, "end": v(478.44, 7363.8) * mm});
            skLineSegment(sketch, "E101.left", {"start": v(1227.74, 8964) * mm, "end": v(1227.74, 7363.8) * mm});
            skLineSegment(sketch, "E101.right", {"start": v(478.44, 8964) * mm, "end": v(478.44, 7363.8) * mm});
            skSolve(sketch);
        }
        {
            var Q0;
            Q0=makeQuery(id+"F13.opExtrude","SWEPT_FACE",FACE,{"disambiguationData":[OSD([sQuery(id+"F12.wireOp",EDGE,"E19.top")])]});
            var sketch = newSketch(context, id + "F16", { "sketchPlane" : qUnion([Q0])});
            skLineSegment(sketch, "E102.bottom", {"start": v(15.24, 0) * mm, "end": v(688.34, 0) * mm});
            skLineSegment(sketch, "E102.top", {"start": v(15.24, 50.8) * mm, "end": v(688.34, 50.8) * mm});
            skLineSegment(sketch, "E102.left", {"start": v(15.24, 0) * mm, "end": v(15.24, 50.8) * mm});
            skLineSegment(sketch, "E102.right", {"start": v(688.34, 0) * mm, "end": v(688.34, 50.8) * mm});
            skLineSegment(sketch, "E103.bottom", {"start": v(-1788.16, 0) * mm, "end": v(-2435.86, 0) * mm});
            skLineSegment(sketch, "E103.top", {"start": v(-1788.16, 50.8) * mm, "end": v(-2435.86, 50.8) * mm});
            skLineSegment(sketch, "E103.left", {"start": v(-1788.16, 0) * mm, "end": v(-1788.16, 50.8) * mm});
            skLineSegment(sketch, "E103.right", {"start": v(-2435.86, 0) * mm, "end": v(-2435.86, 50.8) * mm});
            skSolve(sketch);
        }
        {
            var Q0;
            Q0 = qSketchRegion(id + "F16", true);
            extrude(context, id + "F17", {"entities" : qUnion([Q0]), "operationType" : NewBodyOperationType.REMOVE, "endBound" : BoundingType.THROUGH_ALL, "oppositeDirection" : true, "depth" : 25.4 * mm});
        }
        {
            var Q0;
            Q0=makeQuery(id+"F9.opExtrude","CAP_FACE",FACE,{"disambiguationData":[OSD([sQuery(id+"F8.wireOp",EDGE,"E12.bottom"),sQuery(id+"F8.wireOp",EDGE,"E12.top"),sQuery(id+"F8.wireOp",EDGE,"E12.left"),sQuery(id+"F8.wireOp",EDGE,"E12.right")])],"isStart":true});
            var sketch = newSketch(context, id + "F18", { "sketchPlane" : qUnion([Q0])});
            skLineSegment(sketch, "E104.24", {"start": v(2665.63, 7031.21) * mm, "end": v(3414.93, 7031.21) * mm});
            skLineSegment(sketch, "E104.25", {"start": v(2665.63, 8631.41) * mm, "end": v(3414.93, 8631.41) * mm});
            skLineSegment(sketch, "E104.26", {"start": v(2665.63, 7031.21) * mm, "end": v(2665.63, 8631.41) * mm});
            skLineSegment(sketch, "E104.27", {"start": v(3414.93, 7031.21) * mm, "end": v(3414.93, 8631.41) * mm});
            skLineSegment(sketch, "E104.36", {"start": v(-2004.06, 963.1) * mm, "end": v(-2004.06, 3910.58) * mm});
            skArc(sketch, "E104.37", {"start": v(-2004.06, 3910.58) * mm, "mid": v(-1922.23, 4108.15) * mm, "end": v(-1724.66, 4189.98) * mm});
            skLineSegment(sketch, "E104.38", {"start": v(-2004.06, 963.1) * mm, "end": v(-1800.86, 963.1) * mm});
            skLineSegment(sketch, "E104.39", {"start": v(-1800.86, 963.1) * mm, "end": v(-1800.86, 3910.58) * mm});
            skArc(sketch, "E104.40", {"start": v(-1800.86, 3910.58) * mm, "mid": v(-1778.54, 3964.47) * mm, "end": v(-1724.66, 3986.78) * mm});
            skLineSegment(sketch, "E104.41", {"start": v(-1724.66, 3986.78) * mm, "end": v(3872.3, 3986.78) * mm});
            skLineSegment(sketch, "E104.42", {"start": v(-1724.66, 4189.98) * mm, "end": v(3872.3, 4189.98) * mm});
            skLineSegment(sketch, "E104.43", {"start": v(-1778.54, 3964.47) * mm, "end": v(-1922.23, 4108.15) * mm});
            skLineSegment(sketch, "E104.44", {"start": v(-2423.16, 3139.03) * mm, "end": v(-2219.96, 3139.03) * mm});
            skLineSegment(sketch, "E104.45", {"start": v(-2219.96, 3139.03) * mm, "end": v(-2219.96, 4139.18) * mm});
            skArc(sketch, "E104.46", {"start": v(-2219.96, 4139.18) * mm, "mid": v(-2197.64, 4193.07) * mm, "end": v(-2143.76, 4215.38) * mm});
            skLineSegment(sketch, "E104.47", {"start": v(-2423.16, 3139.03) * mm, "end": v(-2423.16, 4139.18) * mm});
            skArc(sketch, "E104.48", {"start": v(-2423.16, 4139.18) * mm, "mid": v(-2341.33, 4336.75) * mm, "end": v(-2143.76, 4418.58) * mm});
            skLineSegment(sketch, "E104.49", {"start": v(-2143.76, 4215.38) * mm, "end": v(3879.27, 4215.38) * mm});
            skLineSegment(sketch, "E104.50", {"start": v(3879.27, 4215.38) * mm, "end": v(3879.27, 4418.58) * mm});
            skLineSegment(sketch, "E104.51", {"start": v(3879.27, 4418.58) * mm, "end": v(-2143.76, 4418.58) * mm});
            skLineSegment(sketch, "E104.52", {"start": v(-2197.64, 4193.07) * mm, "end": v(-2341.33, 4336.75) * mm});
            skLineSegment(sketch, "E104.53", {"start": v(459.74, 993.21) * mm, "end": v(459.74, 3453.38) * mm});
            skArc(sketch, "E104.54", {"start": v(459.74, 3453.38) * mm, "mid": v(541.57, 3650.95) * mm, "end": v(739.14, 3732.78) * mm});
            skLineSegment(sketch, "E104.55", {"start": v(459.74, 993.21) * mm, "end": v(662.94, 993.21) * mm});
            skLineSegment(sketch, "E104.56", {"start": v(662.94, 993.21) * mm, "end": v(662.94, 3453.38) * mm});
            skArc(sketch, "E104.57", {"start": v(662.94, 3453.38) * mm, "mid": v(685.26, 3507.27) * mm, "end": v(739.14, 3529.58) * mm});
            skLineSegment(sketch, "E104.58", {"start": v(739.14, 3529.58) * mm, "end": v(3914.38, 3529.58) * mm});
            skLineSegment(sketch, "E104.59", {"start": v(739.14, 3732.78) * mm, "end": v(3914.38, 3732.78) * mm});
            skLineSegment(sketch, "E104.60", {"start": v(685.26, 3507.27) * mm, "end": v(541.57, 3650.95) * mm});
            skLineSegment(sketch, "E104.61", {"start": v(40.64, 3024.4) * mm, "end": v(243.84, 3024.4) * mm});
            skLineSegment(sketch, "E104.62", {"start": v(243.84, 3024.4) * mm, "end": v(243.84, 3681.98) * mm});
            skArc(sketch, "E104.63", {"start": v(243.84, 3681.98) * mm, "mid": v(266.16, 3735.87) * mm, "end": v(320.04, 3758.18) * mm});
            skLineSegment(sketch, "E104.64", {"start": v(40.64, 3024.4) * mm, "end": v(40.64, 3681.98) * mm});
            skArc(sketch, "E104.65", {"start": v(40.64, 3681.98) * mm, "mid": v(122.47, 3879.55) * mm, "end": v(320.04, 3961.38) * mm});
            skLineSegment(sketch, "E104.66", {"start": v(320.04, 3758.18) * mm, "end": v(3899.59, 3758.18) * mm});
            skLineSegment(sketch, "E104.67", {"start": v(3899.59, 3758.18) * mm, "end": v(3899.59, 3961.38) * mm});
            skLineSegment(sketch, "E104.68", {"start": v(3899.59, 3961.38) * mm, "end": v(320.04, 3961.38) * mm});
            skLineSegment(sketch, "E104.69", {"start": v(266.16, 3735.87) * mm, "end": v(122.47, 3879.55) * mm});
            skLineSegment(sketch, "E104.70", {"start": v(3914.38, 3732.78) * mm, "end": v(3914.38, 3529.58) * mm});
            skLineSegment(sketch, "E104.71", {"start": v(3872.3, 3986.78) * mm, "end": v(3872.3, 4189.98) * mm});
            skLineSegment(sketch, "E104.72", {"start": v(-1832.37, 4443.98) * mm, "end": v(4264.41, 4443.98) * mm});
            skArc(sketch, "E104.73", {"start": v(-2219.96, 4748.78) * mm, "mid": v(-2197.64, 4694.9) * mm, "end": v(-2143.76, 4672.58) * mm});
            skArc(sketch, "E104.74", {"start": v(662.94, 5434.58) * mm, "mid": v(685.26, 5380.7) * mm, "end": v(739.14, 5358.38) * mm});
            skArc(sketch, "E104.75", {"start": v(243.84, 5205.98) * mm, "mid": v(266.16, 5152.1) * mm, "end": v(320.04, 5129.78) * mm});
            skLineSegment(sketch, "E104.76", {"start": v(3899.59, 5129.78) * mm, "end": v(3899.59, 4926.58) * mm});
            skLineSegment(sketch, "E104.77", {"start": v(3879.27, 4672.58) * mm, "end": v(3879.27, 4469.38) * mm});
            skLineSegment(sketch, "E104.78", {"start": v(3914.38, 5155.18) * mm, "end": v(3914.38, 5358.38) * mm});
            skLineSegment(sketch, "E104.79", {"start": v(685.26, 5380.7) * mm, "end": v(541.57, 5237.02) * mm});
            skArc(sketch, "E104.80", {"start": v(40.64, 5205.98) * mm, "mid": v(122.47, 5008.42) * mm, "end": v(320.04, 4926.58) * mm});
            skLineSegment(sketch, "E104.81", {"start": v(-2143.76, 4672.58) * mm, "end": v(-611.16, 4672.58) * mm});
            skLineSegment(sketch, "E104.82", {"start": v(-2197.64, 4694.9) * mm, "end": v(-2341.33, 4551.22) * mm});
            skArc(sketch, "E104.83", {"start": v(-2423.16, 4748.78) * mm, "mid": v(-2341.33, 4551.22) * mm, "end": v(-2143.76, 4469.38) * mm});
            skLineSegment(sketch, "E104.84", {"start": v(266.16, 5152.1) * mm, "end": v(122.47, 5008.42) * mm});
            skArc(sketch, "E104.85", {"start": v(459.74, 5434.58) * mm, "mid": v(541.57, 5237.02) * mm, "end": v(739.14, 5155.18) * mm});
            skLineSegment(sketch, "E104.86", {"start": v(320.04, 5129.78) * mm, "end": v(3899.59, 5129.78) * mm});
            skLineSegment(sketch, "E104.87", {"start": v(739.14, 5155.18) * mm, "end": v(3914.38, 5155.18) * mm});
            skLineSegment(sketch, "E104.88", {"start": v(3879.27, 4469.38) * mm, "end": v(-2143.76, 4469.38) * mm});
            skLineSegment(sketch, "E104.89", {"start": v(739.14, 5358.38) * mm, "end": v(3914.38, 5358.38) * mm});
            skLineSegment(sketch, "E104.90", {"start": v(3899.59, 4926.58) * mm, "end": v(320.04, 4926.58) * mm});
            skLineSegment(sketch, "E104.91", {"start": v(-2423.16, 4748.78) * mm, "end": v(-2423.16, 6609.89) * mm});
            skLineSegment(sketch, "E104.92", {"start": v(-2423.16, 6609.89) * mm, "end": v(-2219.96, 6609.89) * mm});
            skLineSegment(sketch, "E104.93", {"start": v(-2219.96, 6609.89) * mm, "end": v(-2219.96, 4748.78) * mm});
            skLineSegment(sketch, "E104.94", {"start": v(40.64, 5205.98) * mm, "end": v(40.64, 6602.13) * mm});
            skLineSegment(sketch, "E104.95", {"start": v(40.64, 6602.13) * mm, "end": v(243.84, 6602.13) * mm});
            skLineSegment(sketch, "E104.96", {"start": v(243.84, 6602.13) * mm, "end": v(243.84, 5205.98) * mm});
            skLineSegment(sketch, "E104.97", {"start": v(459.74, 5434.58) * mm, "end": v(459.74, 7694.34) * mm});
            skLineSegment(sketch, "E104.98", {"start": v(459.74, 7694.34) * mm, "end": v(662.94, 7694.34) * mm});
            skLineSegment(sketch, "E104.99", {"start": v(662.94, 7694.34) * mm, "end": v(662.94, 5434.58) * mm});
            skLineSegment(sketch, "E104.100", {"start": v(-1817.3, 7728.89) * mm, "end": v(-2020.5, 7728.89) * mm});
            skLineSegment(sketch, "E104.101", {"start": v(-2020.5, 7728.89) * mm, "end": v(-2020.5, 5361.81) * mm});
            skLineSegment(sketch, "E104.102", {"start": v(-1817.3, 7728.89) * mm, "end": v(-1817.3, 5361.81) * mm});
            skArc(sketch, "E104.103", {"start": v(-2020.5, 5361.81) * mm, "mid": v(-1890.04, 5046.85) * mm, "end": v(-1575.08, 4916.4) * mm});
            skArc(sketch, "E104.104", {"start": v(-1817.3, 5361.81) * mm, "mid": v(-1746.36, 5190.54) * mm, "end": v(-1575.08, 5119.6) * mm});
            skLineSegment(sketch, "E104.105", {"start": v(-1575.08, 4916.4) * mm, "end": v(-1413.46, 4916.4) * mm});
            skLineSegment(sketch, "E104.106", {"start": v(-1575.08, 5119.6) * mm, "end": v(-1383.27, 5119.6) * mm});
            skLineSegment(sketch, "E104.107", {"start": v(-1746.36, 5190.54) * mm, "end": v(-1890.04, 5046.85) * mm});
            skLineSegment(sketch, "E104.108", {"start": v(-1727.68, 5119.6) * mm, "end": v(-1727.68, 4916.4) * mm});
            skPoint(sketch, "E104.109", {"position": v(-1494.27, 4916.4) * mm});
            skLineSegment(sketch, "E104.110", {"start": v(-1413.46, 4916.4) * mm, "end": v(-611.16, 4672.58) * mm});
            skLineSegment(sketch, "E104.111", {"start": v(-1383.27, 5119.6) * mm, "end": v(87.7, 4672.58) * mm});
            skLineSegment(sketch, "E104.112", {"start": v(-606.43, 4671.15) * mm, "end": v(-547.34, 4865.57) * mm});
            skLineSegment(sketch, "E104.113", {"start": v(87.7, 4672.58) * mm, "end": v(3879.27, 4672.58) * mm});
            skSolve(sketch);
        }
        {
            var Q0;
            Q0 = qSketchRegion(id + "F18", true);
            extrude(context, id + "F19", {"entities" : qUnion([Q0]), "depth" : 50.8 * mm});
        }
    });
